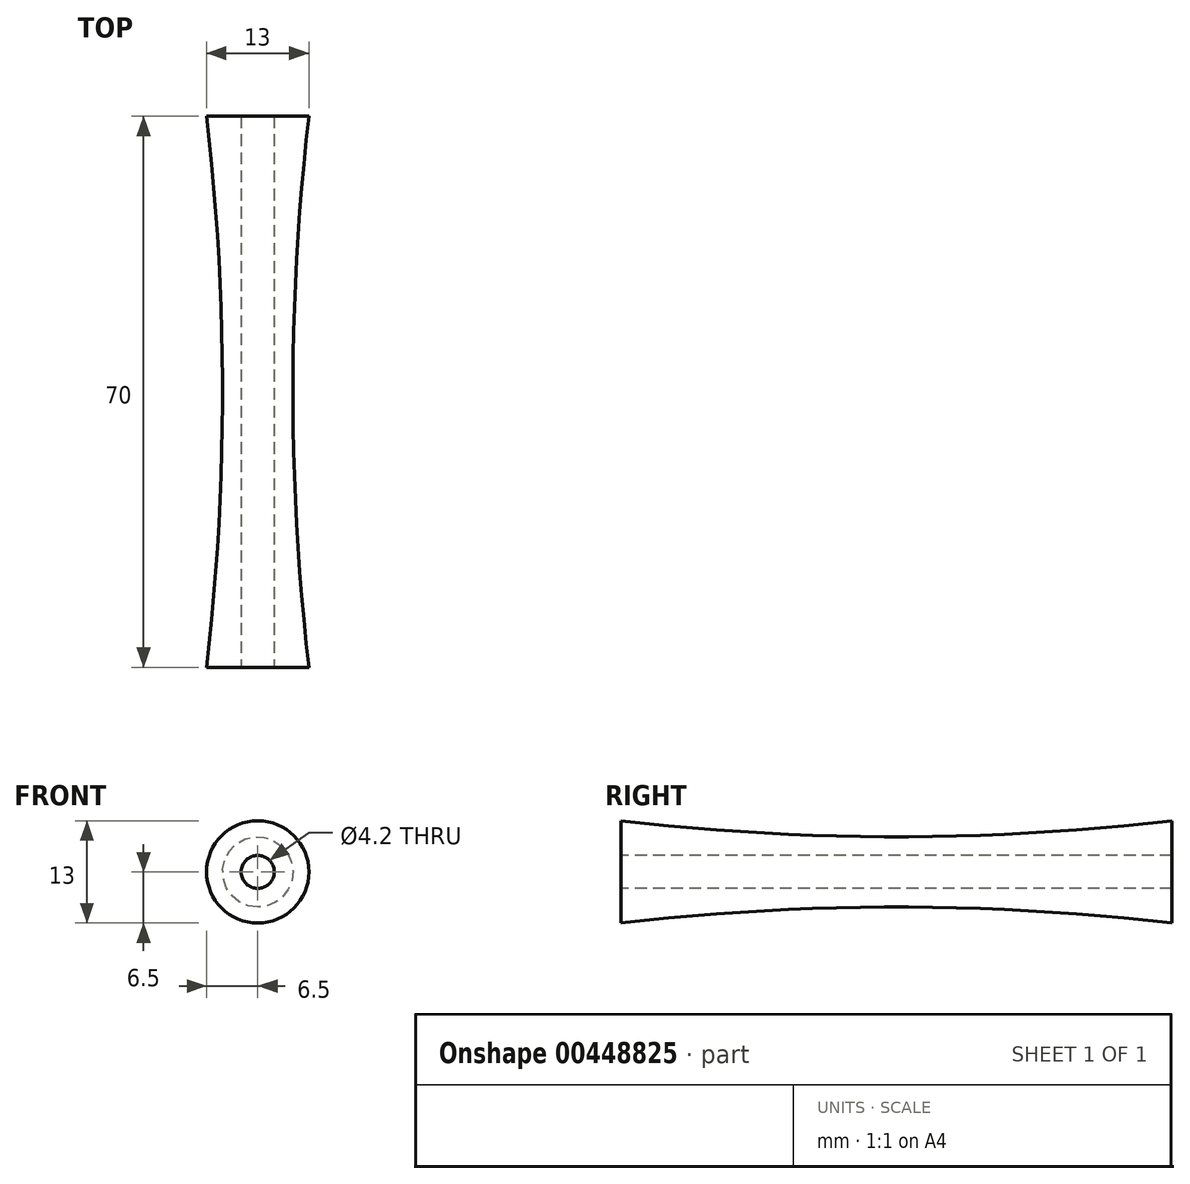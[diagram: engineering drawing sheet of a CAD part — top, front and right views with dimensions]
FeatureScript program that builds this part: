
annotation { "Feature Type Name" : "Feature", "Feature Type Description" : "" }
export const myFeature = defineFeature(function(context is Context, id is Id, definition is map)
    precondition{}
    {
        {
            var Q0;
            Q0=qCreatedBy(makeId("Top.planeOp"),FACE);
            var sketch = newSketch(context, id + "F0", { "sketchPlane" : qUnion([Q0])});
            skLineSegment(sketch, "E0", {"start": v(0, 0) * mm, "end": v(0, 70) * mm});
            skLineSegment(sketch, "E1", {"start": v(0, 70) * mm, "end": v(6.5, 70) * mm, "construction": true});
            skLineSegment(sketch, "E2", {"start": v(6.5, 70) * mm, "end": v(6.5, 0) * mm, "construction": true});
            skLineSegment(sketch, "E3", {"start": v(6.5, 0) * mm, "end": v(0, 0) * mm, "construction": true});
            skLineSegment(sketch, "E4", {"start": v(2.1, 70) * mm, "end": v(2.1, 0) * mm});
            skArc(sketch, "E5", {"start": v(6.5, 70) * mm, "mid": v(4.47, 35) * mm, "end": v(6.5, 0) * mm});
            skPoint(sketch, "E5.centerSnap0", {"position": v(6.5, 35) * mm});
            skLineSegment(sketch, "E6", {"start": v(2.1, 70) * mm, "end": v(6.5, 70) * mm});
            skLineSegment(sketch, "E7", {"start": v(2.1, 0) * mm, "end": v(6.5, 0) * mm});
            skSolve(sketch);
        }
        {
            var Q0;
            Q0=makeQuery(id+"F0.imprint","IMPRINT",FACE,{"disambiguationData":[TD([[makeQuery(id+"F0.imprint","IMPRINT",EDGE,{"derivedFrom":sQuery(id+"F0.wireOp",EDGE,"E4")}),1.0]])]});
            var Q1;
            Q1=sQuery(id+"F0.wireOp",EDGE,"E0");
            revolve(context, id + "F1", {"surfaceOperationType" : NewSurfaceOperationType.NEW, "entities" : qUnion([Q0]), "axis" : qUnion([Q1]), "revolveType" : RevolveType.FULL});
        }
    });
